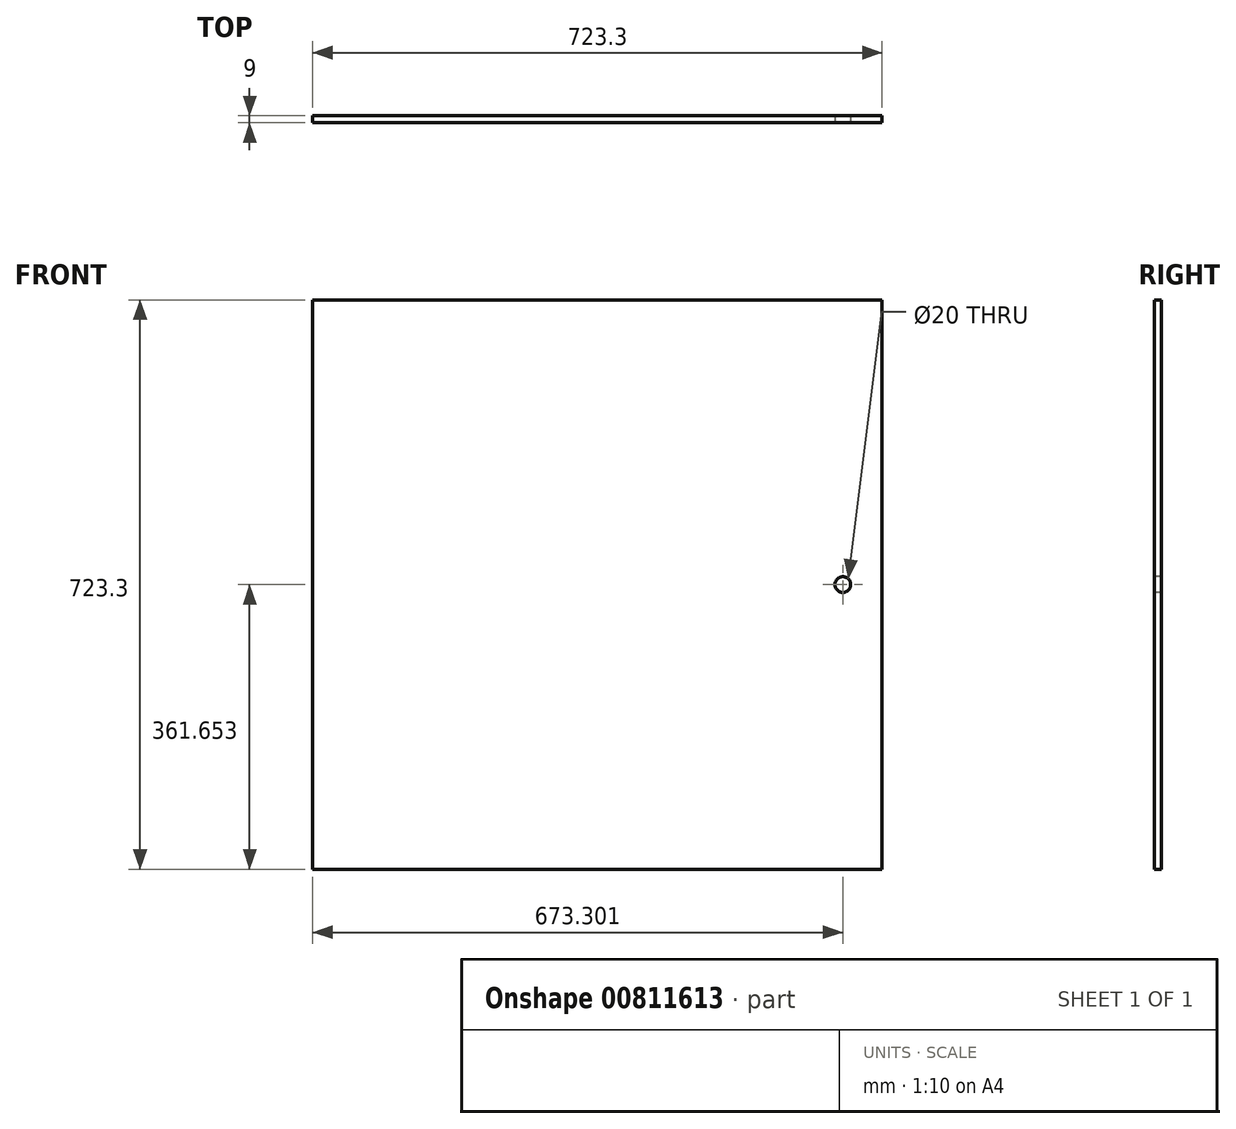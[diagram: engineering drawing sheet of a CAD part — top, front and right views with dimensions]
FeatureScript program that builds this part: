
annotation { "Feature Type Name" : "Feature", "Feature Type Description" : "" }
export const myFeature = defineFeature(function(context is Context, id is Id, definition is map)
    precondition{}
    {
        {
            var Q0;
            Q0=qCreatedBy(makeId("Front.planeOp"),FACE);
            var sketch = newSketch(context, id + "F0", { "sketchPlane" : qUnion([Q0])});
            skLineSegment(sketch, "E0.bottom", {"start": v(-61.6, 675.73) * mm, "end": v(661.7, 675.73) * mm});
            skLineSegment(sketch, "E0.top", {"start": v(-61.6, -47.57) * mm, "end": v(661.7, -47.57) * mm});
            skLineSegment(sketch, "E0.left", {"start": v(-61.6, 675.73) * mm, "end": v(-61.6, -47.57) * mm});
            skLineSegment(sketch, "E0.right", {"start": v(661.7, 675.73) * mm, "end": v(661.7, -47.57) * mm});
            skSolve(sketch);
        }
        {
            var Q0;
            Q0 = qSketchRegion(id + "F0", true);
            extrude(context, id + "F1", {"entities" : qUnion([Q0]), "depth" : 9 * mm, "offsetDistance" : 25 * mm});
        }
        {
            var Q0;
            Q0=makeQuery(id+"F1.opExtrude","CAP_FACE",FACE,{"disambiguationData":[OSD([sQuery(id+"F0.wireOp",EDGE,"E0.bottom"),sQuery(id+"F0.wireOp",EDGE,"E0.top"),sQuery(id+"F0.wireOp",EDGE,"E0.left"),sQuery(id+"F0.wireOp",EDGE,"E0.right")])],"isStart":false});
            var sketch = newSketch(context, id + "F2", { "sketchPlane" : qUnion([Q0])});
            skLineSegment(sketch, "E1", {"start": v(661.7, 314.08) * mm, "end": v(611.7, 314.08) * mm});
            skCircle(sketch, "E2", {"center": v(611.7, 314.08) * mm, "radius": 10 * mm});
            skSolve(sketch);
        }
        {
            var Q0;
            Q0 = qSketchRegion(id + "F2", true);
            extrude(context, id + "F3", {"entities" : qUnion([Q0]), "operationType" : NewBodyOperationType.REMOVE, "oppositeDirection" : true, "depth" : 25 * mm, "offsetDistance" : 25 * mm});
        }
    });
